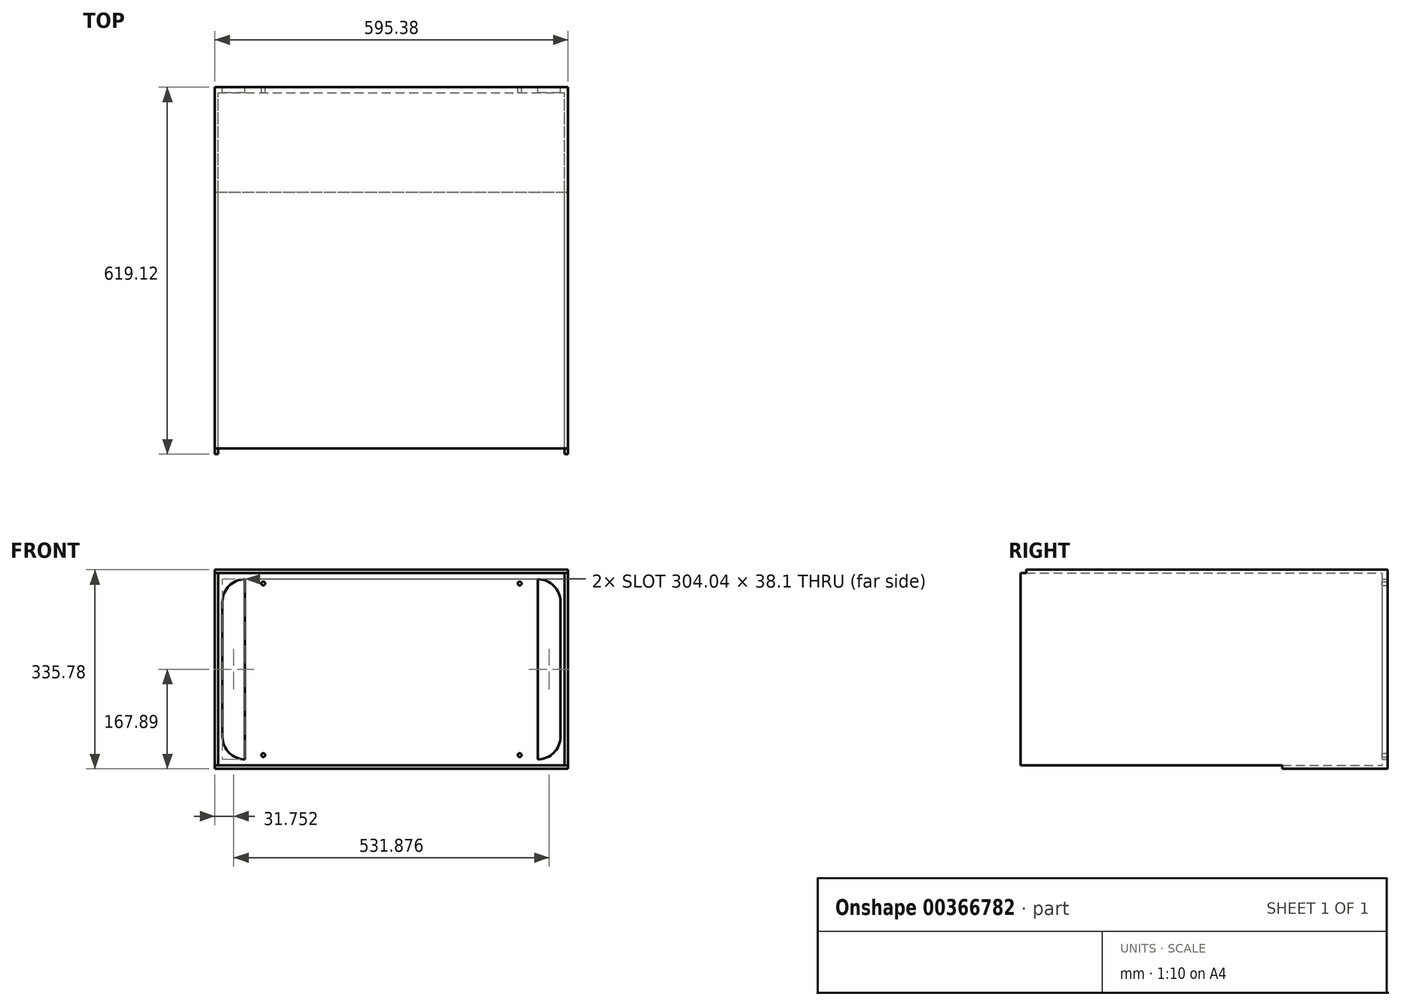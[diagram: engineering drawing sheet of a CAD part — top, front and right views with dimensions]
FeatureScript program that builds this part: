
annotation { "Feature Type Name" : "Feature", "Feature Type Description" : "" }
export const myFeature = defineFeature(function(context is Context, id is Id, definition is map)
    precondition{}
    {
        {
            var Q0;
            Q0=qCreatedBy(makeId("Front.planeOp"),FACE);
            var sketch = newSketch(context, id + "F0", { "sketchPlane" : qUnion([Q0])});
            skLineSegment(sketch, "E0.bottom", {"start": v(297.69, 167.9) * mm, "end": v(-297.69, 167.9) * mm});
            skLineSegment(sketch, "E0.top", {"start": v(297.69, -167.9) * mm, "end": v(-297.69, -167.9) * mm});
            skLineSegment(sketch, "E0.left", {"start": v(297.69, 167.9) * mm, "end": v(297.69, -167.9) * mm});
            skLineSegment(sketch, "E0.right", {"start": v(-297.69, 167.9) * mm, "end": v(-297.69, -167.9) * mm});
            skPoint(sketch, "E0.middle", {"position": v(0, 0) * mm});
            skSolve(sketch);
        }
        {
            var Q0;
            Q0=makeQuery(id+"F0.imprint","IMPRINT",FACE,{"disambiguationData":[TD([[makeQuery(id+"F0.imprint","IMPRINT",EDGE,{"derivedFrom":sQuery(id+"F0.wireOp",EDGE,"E0.bottom")}),1.0]])]});
            extrude(context, id + "F1", {"entities" : qUnion([Q0]), "endBound" : BoundingType.SYMMETRIC, "depth" : 9.52 * mm});
        }
        {
            var Q0;
            Q0=makeQuery(id+"F1.opExtrude","CAP_FACE",FACE,{"disambiguationData":[OSD([sQuery(id+"F0.wireOp",EDGE,"E0.bottom"),sQuery(id+"F0.wireOp",EDGE,"E0.top"),sQuery(id+"F0.wireOp",EDGE,"E0.left"),sQuery(id+"F0.wireOp",EDGE,"E0.right")])],"isStart":false});
            var sketch = newSketch(context, id + "F2", { "sketchPlane" : qUnion([Q0])});
            skLineSegment(sketch, "E1", {"start": v(-292.1, 162.3) * mm, "end": v(-297.69, 162.3) * mm});
            skLineSegment(sketch, "E2", {"start": v(292.1, 162.3) * mm, "end": v(297.69, 162.3) * mm});
            skLineSegment(sketch, "E3", {"start": v(-297.69, 162.3) * mm, "end": v(-297.69, -162.3) * mm});
            skLineSegment(sketch, "E4", {"start": v(-297.69, -162.3) * mm, "end": v(-292.1, -162.3) * mm});
            skLineSegment(sketch, "E5", {"start": v(-292.1, 162.3) * mm, "end": v(-292.1, -162.3) * mm});
            skLineSegment(sketch, "E6", {"start": v(292.1, 162.3) * mm, "end": v(292.1, -162.3) * mm});
            skLineSegment(sketch, "E7", {"start": v(292.1, -162.3) * mm, "end": v(297.69, -162.3) * mm});
            skLineSegment(sketch, "E8", {"start": v(297.69, -162.3) * mm, "end": v(297.69, 162.3) * mm});
            skSolve(sketch);
        }
        {
            var Q0;
            Q0 = qSketchRegion(id + "F2", true);
            extrude(context, id + "F3", {"entities" : qUnion([Q0]), "operationType" : NewBodyOperationType.ADD, "depth" : 609.6 * mm});
        }
        {
            var Q0;
            Q0=makeQuery(id+"F1.opExtrude","CAP_FACE",FACE,{"disambiguationData":[OSD([sQuery(id+"F0.wireOp",EDGE,"E0.bottom"),sQuery(id+"F0.wireOp",EDGE,"E0.top"),sQuery(id+"F0.wireOp",EDGE,"E0.left"),sQuery(id+"F0.wireOp",EDGE,"E0.right")])],"isStart":false});
            var sketch = newSketch(context, id + "F4", { "sketchPlane" : qUnion([Q0])});
            skLineSegment(sketch, "E9.bottom", {"start": v(-297.69, 167.9) * mm, "end": v(297.69, 167.9) * mm});
            skLineSegment(sketch, "E9.top", {"start": v(-297.69, 162.3) * mm, "end": v(297.69, 162.3) * mm});
            skLineSegment(sketch, "E9.left", {"start": v(-297.69, 167.9) * mm, "end": v(-297.69, 162.3) * mm});
            skLineSegment(sketch, "E9.right", {"start": v(297.69, 167.9) * mm, "end": v(297.69, 162.3) * mm});
            skSolve(sketch);
        }
        {
            var Q0;
            Q0=makeQuery(id+"F3.opExtrude","CAP_FACE",FACE,{"disambiguationData":[OSD([sQuery(id+"F2.wireOp",EDGE,"WzK90LZb-VVzD-1Ku5-vK76-Iu93OcMhjfYS"),sQuery(id+"F2.wireOp",EDGE,"AgrCebdF-qPDm-ZDMO-hTSJ-PPNefHA11mKc"),sQuery(id+"F2.wireOp",EDGE,"E1"),sQuery(id+"F2.wireOp",EDGE,"ogT1xFXn-eRBR-EJWY-r0ix-9z1bJXZTEV3T")])],"isStart":false});
            cPlane(context, id + "F5", {"entities" : qUnion([Q0]), "cplaneType" : CPlaneType.OFFSET, "offset" : 9.52 * mm, "oppositeDirection" : true, "width" : 152.4 * mm, "height" : 152.4 * mm});
        }
        {
            var Q0;
            Q0 = qSketchRegion(id + "F4", true);
            var Q1;
            Q1=qCreatedBy(id+"F5.planeOp",FACE);
            extrude(context, id + "F6", {"entities" : qUnion([Q0]), "operationType" : NewBodyOperationType.ADD, "endBound" : BoundingType.UP_TO_SURFACE, "endBoundEntityFace" : qUnion([Q1]), "depth" : 25.4 * mm});
        }
        {
            var Q0;
            Q0=makeQuery(id+"F1.opExtrude","CAP_FACE",FACE,{"disambiguationData":[OSD([sQuery(id+"F0.wireOp",EDGE,"E0.bottom"),sQuery(id+"F0.wireOp",EDGE,"E0.top"),sQuery(id+"F0.wireOp",EDGE,"E0.left"),sQuery(id+"F0.wireOp",EDGE,"E0.right")])],"isStart":true});
            var sketch = newSketch(context, id + "F7", { "sketchPlane" : qUnion([Q0])});
            skLineSegment(sketch, "E10.bottom", {"start": v(-297.69, -167.9) * mm, "end": v(297.69, -167.9) * mm});
            skLineSegment(sketch, "E10.top", {"start": v(-297.69, -162.3) * mm, "end": v(297.69, -162.3) * mm});
            skLineSegment(sketch, "E10.left", {"start": v(-297.69, -167.9) * mm, "end": v(-297.69, -162.3) * mm});
            skLineSegment(sketch, "E10.right", {"start": v(297.69, -167.9) * mm, "end": v(297.69, -162.3) * mm});
            skSolve(sketch);
        }
        {
            var Q0;
            Q0 = qSketchRegion(id + "F7", true);
            extrude(context, id + "F8", {"entities" : qUnion([Q0]), "operationType" : NewBodyOperationType.ADD, "oppositeDirection" : true, "depth" : 177.8 * mm});
        }
        {
            var Q0;
            Q0=makeQuery(id+"F1.opExtrude","CAP_FACE",FACE,{"disambiguationData":[OSD([sQuery(id+"F0.wireOp",EDGE,"E0.bottom"),sQuery(id+"F0.wireOp",EDGE,"E0.top"),sQuery(id+"F0.wireOp",EDGE,"E0.left"),sQuery(id+"F0.wireOp",EDGE,"E0.right")])],"isStart":true});
            var sketch = newSketch(context, id + "F9", { "sketchPlane" : qUnion([Q0])});
            skLineSegment(sketch, "E11", {"start": v(-284.99, 113.92) * mm, "end": v(-284.99, -113.92) * mm});
            skLineSegment(sketch, "E12", {"start": v(-246.89, 152.02) * mm, "end": v(-246.89, -152.02) * mm});
            skArc(sketch, "E13", {"start": v(-284.99, 113.92) * mm, "mid": v(-273.83, 140.86) * mm, "end": v(-246.89, 152.02) * mm});
            skArc(sketch, "E14", {"start": v(-284.99, -113.92) * mm, "mid": v(-273.83, -140.86) * mm, "end": v(-246.89, -152.02) * mm});
            skLineSegment(sketch, "E15", {"start": v(-246.89, 152.02) * mm, "end": v(-246.89, 167.9) * mm, "construction": true});
            skLineSegment(sketch, "E16", {"start": v(-246.89, -152.02) * mm, "end": v(-246.89, -167.9) * mm, "construction": true});
            skLineSegment(sketch, "E17", {"start": v(-246.89, 152.02) * mm, "end": v(-297.69, 152.02) * mm, "construction": true});
            skLineSegment(sketch, "E18", {"start": v(0, 0) * mm, "end": v(0, 167.9) * mm, "construction": true});
            skLineSegment(sketch, "E19.MirrorCS", {"start": v(246.89, -152.02) * mm, "end": v(246.89, -167.9) * mm, "construction": true});
            skLineSegment(sketch, "E20.MirrorCS", {"start": v(246.89, 152.02) * mm, "end": v(297.69, 152.02) * mm, "construction": true});
            skLineSegment(sketch, "E21.MirrorCS", {"start": v(246.89, 152.02) * mm, "end": v(246.89, 167.9) * mm, "construction": true});
            skArc(sketch, "E22.MirrorCS", {"start": v(284.99, 113.92) * mm, "mid": v(273.83, 140.86) * mm, "end": v(246.89, 152.02) * mm});
            skLineSegment(sketch, "E23.MirrorCS", {"start": v(284.99, 113.92) * mm, "end": v(284.99, -113.92) * mm});
            skLineSegment(sketch, "E24.MirrorCS", {"start": v(246.89, 152.02) * mm, "end": v(246.89, -152.02) * mm});
            skArc(sketch, "E25.MirrorCS", {"start": v(284.99, -113.92) * mm, "mid": v(273.83, -140.86) * mm, "end": v(246.89, -152.02) * mm});
            skSolve(sketch);
        }
        {
            var Q0;
            Q0 = qSketchRegion(id + "F9", true);
            extrude(context, id + "F10", {"entities" : qUnion([Q0]), "operationType" : NewBodyOperationType.REMOVE, "endBound" : BoundingType.UP_TO_NEXT, "oppositeDirection" : true, "depth" : 25.4 * mm});
        }
        {
            var Q0;
            Q0=makeQuery(id+"F1.opExtrude","CAP_FACE",FACE,{"disambiguationData":[OSD([sQuery(id+"F0.wireOp",EDGE,"E0.bottom"),sQuery(id+"F0.wireOp",EDGE,"E0.top"),sQuery(id+"F0.wireOp",EDGE,"E0.left"),sQuery(id+"F0.wireOp",EDGE,"E0.right")])],"isStart":true});
            var sketch = newSketch(context, id + "F11", { "sketchPlane" : qUnion([Q0])});
            skCircle(sketch, "E26", {"center": v(-216.26, 144.75) * mm, "radius": 3.18 * mm});
            skCircle(sketch, "E27", {"center": v(-216.26, -144.75) * mm, "radius": 3.18 * mm});
            skCircle(sketch, "E28", {"center": v(216.26, 144.75) * mm, "radius": 3.18 * mm});
            skCircle(sketch, "E29", {"center": v(216.26, -144.75) * mm, "radius": 3.18 * mm});
            skLineSegment(sketch, "E30", {"start": v(-216.26, 144.75) * mm, "end": v(-216.26, -144.75) * mm, "construction": true});
            skLineSegment(sketch, "E31", {"start": v(216.26, -144.75) * mm, "end": v(-216.26, -144.75) * mm, "construction": true});
            skLineSegment(sketch, "E32", {"start": v(216.26, -144.75) * mm, "end": v(216.26, 144.75) * mm, "construction": true});
            skLineSegment(sketch, "E33", {"start": v(0, -144.75) * mm, "end": v(0, 0) * mm, "construction": true});
            skLineSegment(sketch, "E34", {"start": v(-216.26, 0) * mm, "end": v(0, 0) * mm, "construction": true});
            skSolve(sketch);
        }
        {
            var Q0;
            Q0 = qSketchRegion(id + "F11", true);
            extrude(context, id + "F12", {"entities" : qUnion([Q0]), "operationType" : NewBodyOperationType.REMOVE, "endBound" : BoundingType.UP_TO_NEXT, "oppositeDirection" : true, "depth" : 25.4 * mm});
        }
    });
